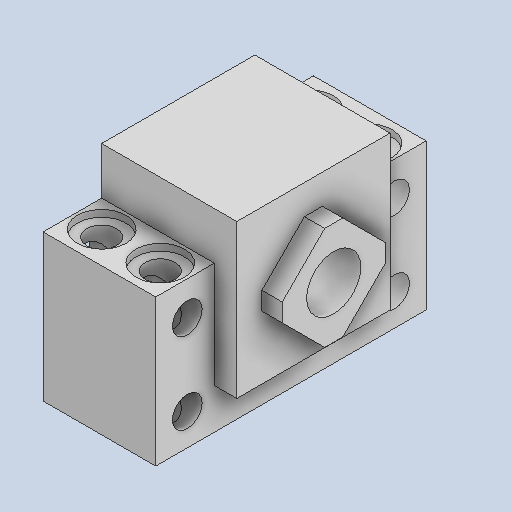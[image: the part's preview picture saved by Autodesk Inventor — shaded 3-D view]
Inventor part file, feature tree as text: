
AUTODESK INVENTOR PART (.ipt)
format: ipt  version: 2023 (Build 270158000, 158)  size: 238,080 bytes
history: native  units: mm
features: extrude x5, sketch x5, pattern_linear x1
ambient origin geometry x8: Origin, YZ Plane, XZ Plane, XY Plane, X Axis, Y Axis, Z Axis, Center Point
bodies: Solid1 (feature_tree)
feature tree (11):
  extrude  "Extrusion1"  Depth=60.0mm
  extrude  "Extrusion2"  Depth=46.0mm
  extrude  "Extrusion3"  Depth=32.5mm
  extrude  "Extrusion4"  Depth=43.0mm
  extrude  "Extrusion5"  Depth=25.0mm TaperAngle=0.0deg
  pattern_linear  "Rectangular Pattern1"  Spacing1=5.0mm  [1 undecoded]
  sketch  "Sketch1"  dims[d0=60.0mm d1=6.6mm]
  sketch  "Sketch2"  dims[d2=18.0mm d3=46.0mm]
  sketch  "Sketch3"  dims[d4=25.0mm d5=32.5mm]
  sketch  "Sketch4"  dims[d6=34.0mm d7=43.0mm]
  sketch  "Sketch5"  dims[d8=12.0mm d9=25.0mm d10=0.0mm d11=5.0mm d12=0.0mm d14=135.0deg d15=19.0mm d16=4.0mm d17=4.5mm d18=0.0mm d19=10.8mm d20=6.0mm d21=7.0mm d22=1.5mm d23=0.0mm d24=6.6mm d25=5.0mm d26=0.0mm d27=20.0mm d29=13.0mm d30=20.0mm d32=-46.0mm]
note: 1 required parameter value undecoded (feature->parameter linkage not recoverable at this tier; creation-order binding heuristic only, values carry confidence <= 0.55)
